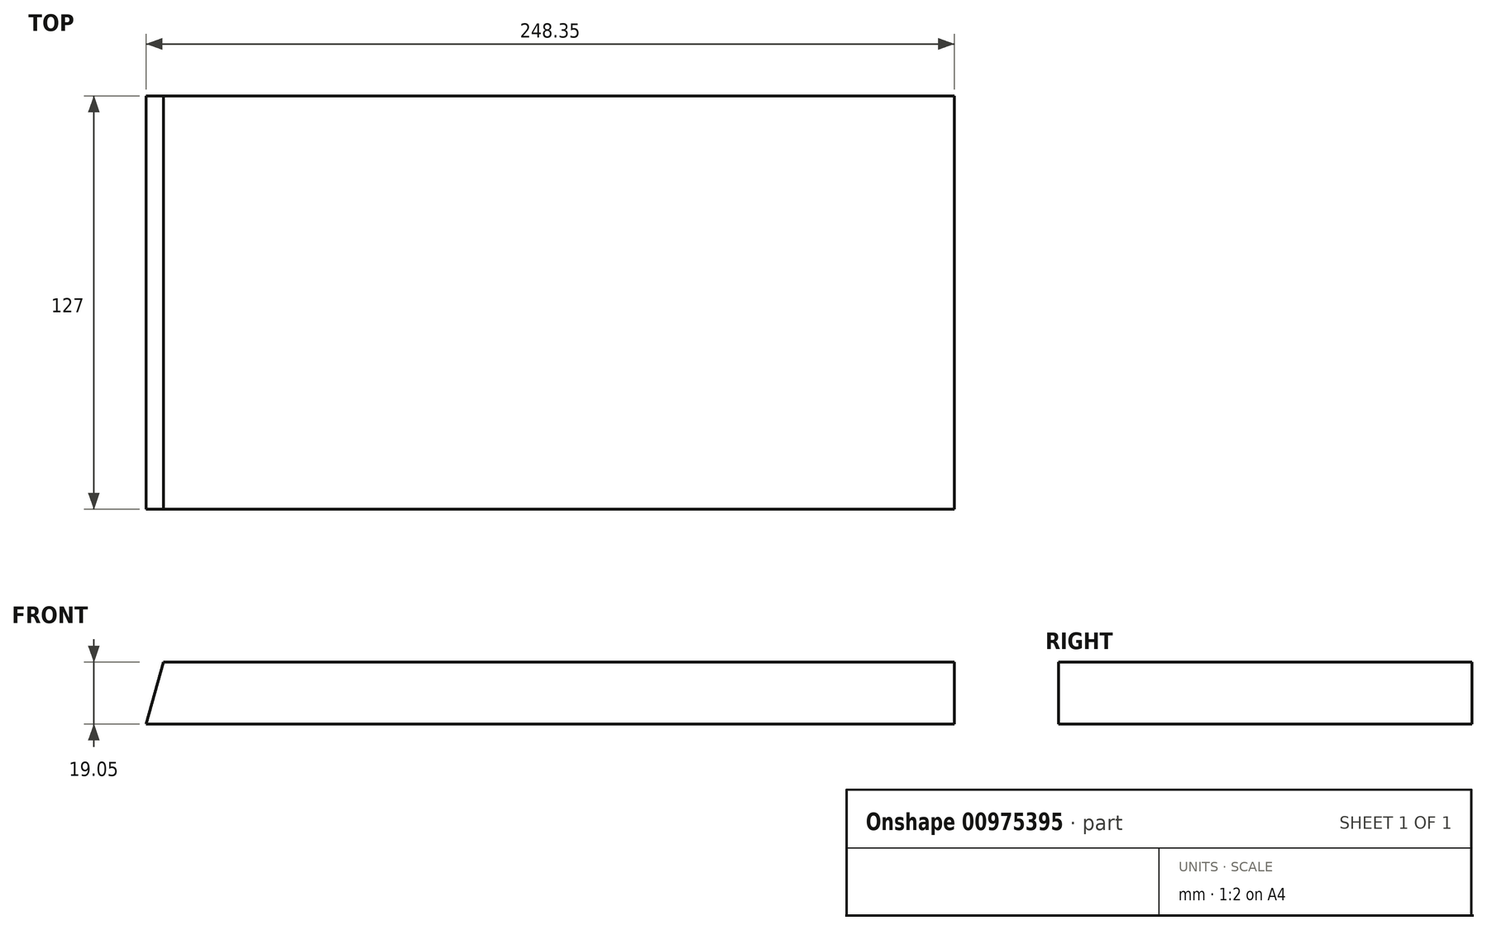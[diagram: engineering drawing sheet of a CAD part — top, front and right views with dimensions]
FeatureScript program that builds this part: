
annotation { "Feature Type Name" : "Feature", "Feature Type Description" : "" }
export const myFeature = defineFeature(function(context is Context, id is Id, definition is map)
    precondition{}
    {
        {
            var Q0;
            Q0=qCreatedBy(makeId("Top.planeOp"),FACE);
            var sketch = newSketch(context, id + "F0", { "sketchPlane" : qUnion([Q0])});
            skLineSegment(sketch, "E0.bottom", {"start": v(-116.56, 42.51) * mm, "end": v(137.44, 42.51) * mm});
            skLineSegment(sketch, "E0.top", {"start": v(-116.56, -84.49) * mm, "end": v(137.44, -84.49) * mm});
            skLineSegment(sketch, "E0.left", {"start": v(-116.56, 42.51) * mm, "end": v(-116.56, -84.49) * mm});
            skLineSegment(sketch, "E0.right", {"start": v(137.44, 42.51) * mm, "end": v(137.44, -84.49) * mm});
            skSolve(sketch);
        }
        {
            var Q0;
            Q0=qSketchRegion(id+"F0",true);
            extrude(context, id + "F1", {"entities" : qUnion([Q0]), "oppositeDirection" : true, "depth" : 19.05 * mm, "offsetDistance" : 25.4 * mm});
        }
        {
            var Q0;
            Q0=makeQuery(id+"F1.opExtrude","SWEPT_FACE",FACE,{"disambiguationData":[OSD([sQuery(id+"F0.wireOp",EDGE,"E0.top")])]});
            var sketch = newSketch(context, id + "F2", { "sketchPlane" : qUnion([Q0])});
            skPoint(sketch, "E1", {"position": v(-116.56, -9.53) * mm});
            skLineSegment(sketch, "E2", {"start": v(-105.56, 0) * mm, "end": v(-116.56, 0) * mm});
            skLineSegment(sketch, "E3", {"start": v(-116.56, 0) * mm, "end": v(-116.56, -19.05) * mm});
            skLineSegment(sketch, "E4", {"start": v(-116.56, -19.05) * mm, "end": v(-110.9, -19.05) * mm});
            skLineSegment(sketch, "E5", {"start": v(-105.56, 0) * mm, "end": v(-110.9, -19.05) * mm});
            skSolve(sketch);
        }
        {
            var Q0;
            Q0=makeQuery(id+"F2.imprint","IMPRINT",FACE,{"disambiguationData":[TD([[makeQuery(id+"F2.imprint","IMPRINT",EDGE,{"derivedFrom":sQuery(id+"F2.wireOp",EDGE,"E2")}),-1.0]])]});
            extrude(context, id + "F3", {"entities" : qUnion([Q0]), "operationType" : NewBodyOperationType.REMOVE, "oppositeDirection" : true, "depth" : 127 * mm, "offsetDistance" : 25.4 * mm});
        }
    });
